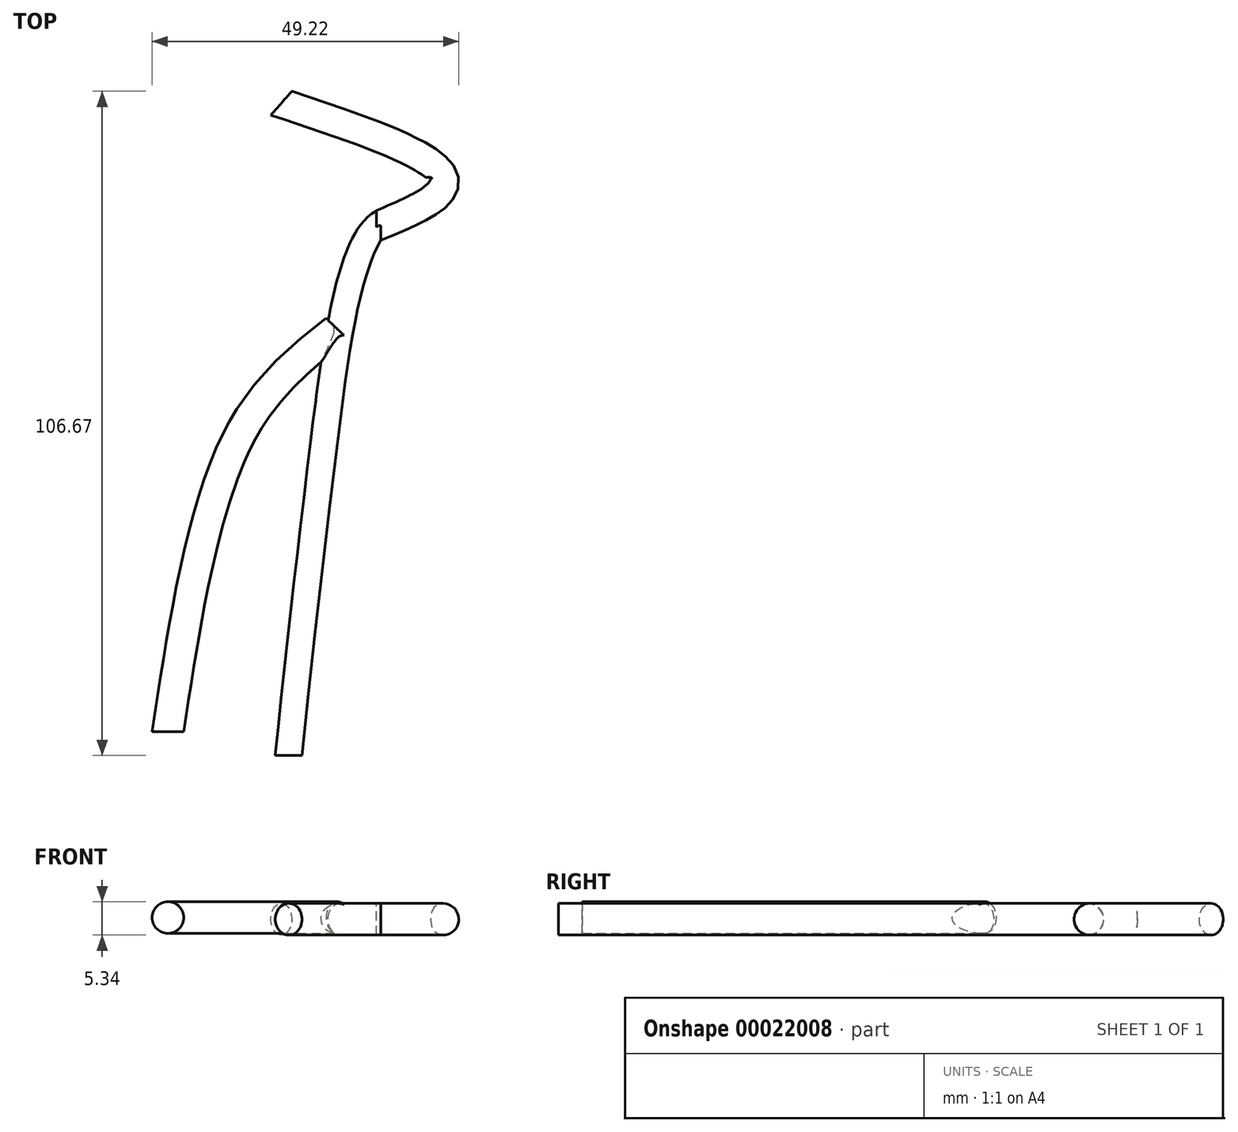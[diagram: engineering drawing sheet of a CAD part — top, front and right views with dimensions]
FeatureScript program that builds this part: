
annotation { "Feature Type Name" : "Feature", "Feature Type Description" : "" }
export const myFeature = defineFeature(function(context is Context, id is Id, definition is map)
    precondition{}
    {
        {
            var Q0;
            Q0=qCreatedBy(makeId("Top.planeOp"),FACE);
            var sketch = newSketch(context, id + "F0", { "sketchPlane" : qUnion([Q0])});
            skFitSpline(sketch, "E0", {"points": [v(0, 0) * mm, v(-21.68, -27.24) * mm, v(-45.64, -424.33) * mm], "startDerivative": vector(-197.47, 310.29) * mm, "endDerivative": vector(-6.39, -667.07) * mm});
            skFitSpline(sketch, "E1", {"points": [v(-18.92, -7.73) * mm, v(-34.56, -24.4) * mm, v(-46.25, -72.1) * mm], "startDerivative": vector(-42.71, -33.06) * mm, "endDerivative": vector(-14, -91.94) * mm});
            skSolve(sketch);
        }
        {
            var Q0;
            Q0=qCreatedBy(makeId("Front.planeOp"),FACE);
            var sketch = newSketch(context, id + "F1", { "sketchPlane" : qUnion([Q0])});
            skCircle(sketch, "E2", {"center": v(0, 0) * mm, "radius": 2.54 * mm});
            skSolve(sketch);
        }
        {
            var Q0;
            Q0=makeQuery(id+"F1.imprint","IMPRINT",FACE,{"disambiguationData":[TD([[makeQuery(id+"F1.imprint","IMPRINT",EDGE,{"derivedFrom":sQuery(id+"F1.wireOp",EDGE,"E2")}),1.0]])]});
            var Q1;
            Q1=sQuery(id+"F0.wireOp",EDGE,"E0");
            sweep(context, id + "F2", {"profiles" : qUnion([Q0]), "path" : qUnion([Q1])});
        }
        {
            var Q0;
            Q0=makeQuery(id+"F2.opSweep","CAP_FACE",FACE,{"disambiguationData":[OSD([sQuery(id+"F0.wireOp",VERTEX,"E0.end"),sQuery(id+"F1.wireOp",EDGE,"E2")])],"isStart":false});
            extrude(context, id + "F3", {"entities" : qUnion([Q0]), "operationType" : NewBodyOperationType.REMOVE, "oppositeDirection" : true, "depth" : 25.4 * mm});
        }
        {
            var Q0;
            Q0=qCreatedBy(makeId("Front.planeOp"),FACE);
            cPlane(context, id + "F4", {"entities" : qUnion([Q0]), "cplaneType" : CPlaneType.OFFSET, "offset" : 152.4 * mm, "width" : 152.4 * mm, "height" : 152.4 * mm});
        }
        {
            var Q0;
            Q0=qCreatedBy(id+"F4.planeOp",FACE);
            var sketch = newSketch(context, id + "F5", { "sketchPlane" : qUnion([Q0])});
            skCircle(sketch, "E3", {"center": v(-5.08, -0.92) * mm, "radius": 82.53 * mm});
            skSolve(sketch);
        }
        {
            var Q0;
            Q0=qSketchRegion(id+"F5",true);
            extrude(context, id + "F6", {"entities" : qUnion([Q0]), "operationType" : NewBodyOperationType.REMOVE, "depth" : 369.5 * mm});
        }
        {
            var Q0;
            Q0=qSketchRegion(id+"F5",true);
            extrude(context, id + "F7", {"entities" : qUnion([Q0]), "operationType" : NewBodyOperationType.REMOVE, "oppositeDirection" : true, "depth" : 76.2 * mm});
        }
        {
            var Q0;
            Q0=qCreatedBy(id+"F4.planeOp",FACE);
            cPlane(context, id + "F8", {"entities" : qUnion([Q0]), "cplaneType" : CPlaneType.OFFSET, "offset" : 80 * mm, "oppositeDirection" : true, "width" : 152.4 * mm, "height" : 152.4 * mm});
        }
        {
            var Q0;
            Q0=qCreatedBy(id+"F8.planeOp",FACE);
            var sketch = newSketch(context, id + "F9", { "sketchPlane" : qUnion([Q0])});
            skCircle(sketch, "E4", {"center": v(-46.56, 0.26) * mm, "radius": 2.54 * mm});
            skSolve(sketch);
        }
        {
            var Q0;
            Q0=makeQuery(id+"F9.imprint","IMPRINT",FACE,{"disambiguationData":[TD([[makeQuery(id+"F9.imprint","IMPRINT",EDGE,{"derivedFrom":sQuery(id+"F9.wireOp",EDGE,"E4")}),1.0]])]});
            var Q1;
            Q1=sQuery(id+"F0.wireOp",EDGE,"E1");
            sweep(context, id + "F10", {"operationType" : NewBodyOperationType.ADD, "profiles" : qUnion([Q0]), "path" : qUnion([Q1])});
        }
        {
            var Q0;
            Q0=qCreatedBy(makeId("Top.planeOp"),FACE);
            var sketch = newSketch(context, id + "F11", { "sketchPlane" : qUnion([Q0])});
            skLineSegment(sketch, "E5.bottom", {"start": v(-12.38, 15.3) * mm, "end": v(15.9, 15.3) * mm});
            skLineSegment(sketch, "E5.top", {"start": v(-12.38, -10.4) * mm, "end": v(15.9, -10.4) * mm});
            skLineSegment(sketch, "E5.left", {"start": v(-12.38, 15.3) * mm, "end": v(-12.38, -10.4) * mm});
            skLineSegment(sketch, "E5.right", {"start": v(15.9, 15.3) * mm, "end": v(15.9, -10.4) * mm});
            skSolve(sketch);
        }
        {
            var Q0;
            Q0 = qSketchRegion(id + "F11", true);
            extrude(context, id + "F12", {"entities" : qUnion([Q0]), "operationType" : NewBodyOperationType.REMOVE, "oppositeDirection" : true, "depth" : 25.4 * mm, "hasSecondDirection" : true, "secondDirectionOppositeDirection" : false, "secondDirectionDepth" : 25.4 * mm});
        }
        {
            var Q0;
            Q0=qCreatedBy(makeId("Top.planeOp"),FACE);
            var sketch = newSketch(context, id + "F13", { "sketchPlane" : qUnion([Q0])});
            skFitSpline(sketch, "E6", {"points": [v(-13.12, 9.2) * mm, v(-2.77, 16.03) * mm, v(-28.64, 28.23) * mm], "startDerivative": vector(39.75, 16.62) * mm, "endDerivative": vector(-63.7, 21.13) * mm});
            skSolve(sketch);
        }
        {
            var Q0;
            Q0=makeQuery(id+"F12.boolean.opBoolean","COPY",FACE,{"derivedFrom":makeQuery(id+"F12.opExtrude","SWEPT_FACE",FACE,{"disambiguationData":[OSD([sQuery(id+"F11.wireOp",EDGE,"E5.left")])]})});
            var Q1;
            Q1=sQuery(id+"F13.wireOp",EDGE,"E6");
            sweep(context, id + "F14", {"operationType" : NewBodyOperationType.ADD, "profiles" : qUnion([Q0]), "path" : qUnion([Q1])});
        }
    });
